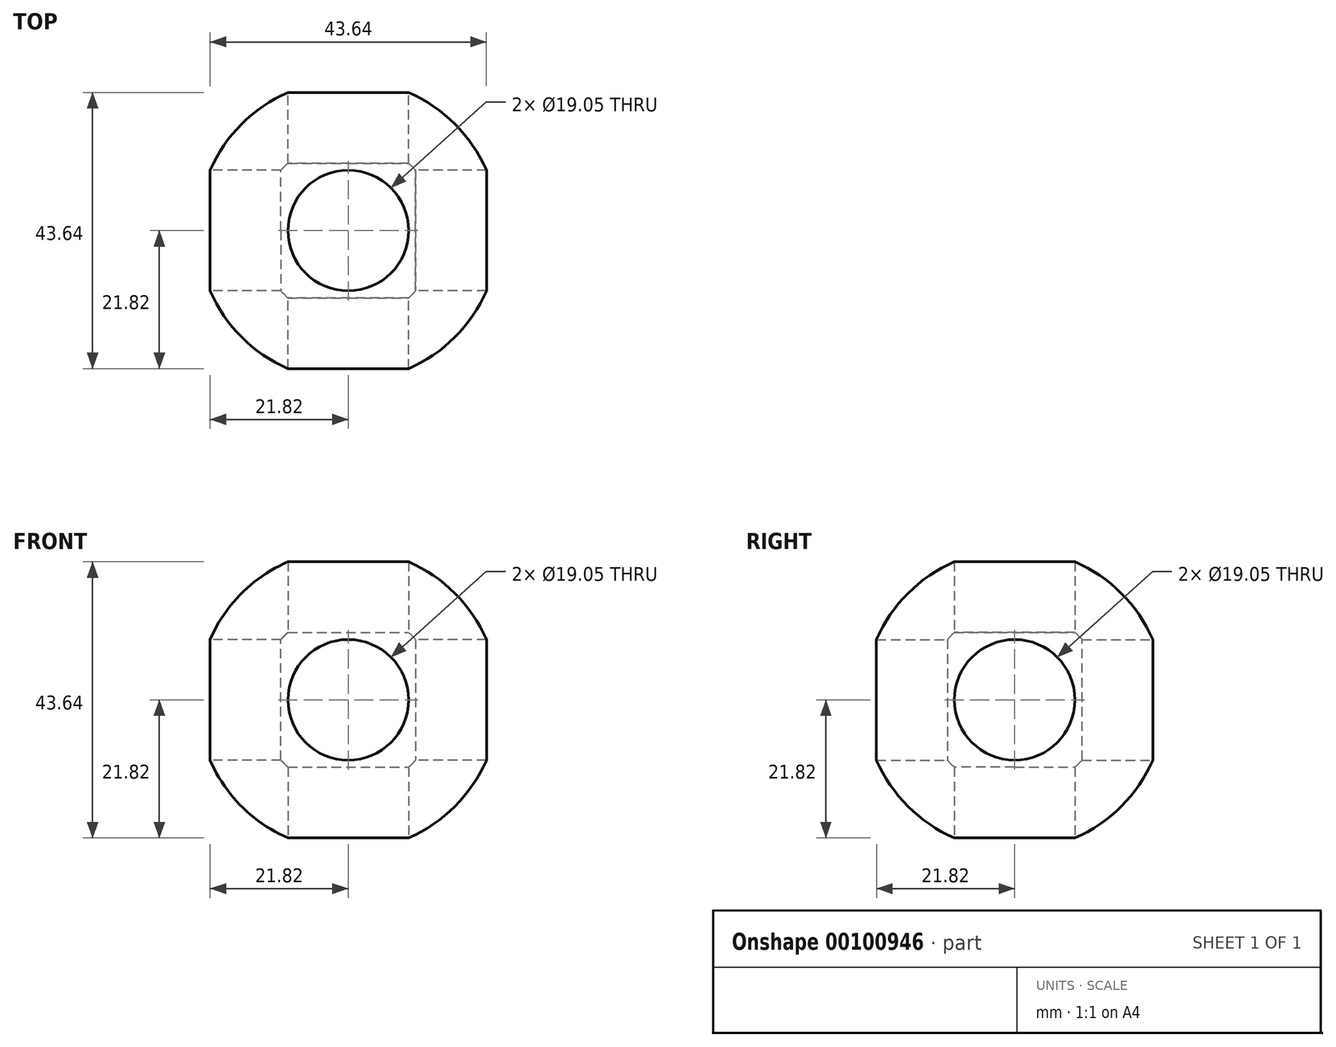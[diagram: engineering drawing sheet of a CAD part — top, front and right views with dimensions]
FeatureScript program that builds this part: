
annotation { "Feature Type Name" : "Feature", "Feature Type Description" : "" }
export const myFeature = defineFeature(function(context is Context, id is Id, definition is map)
    precondition{}
    {
        {
            var Q0;
            Q0=qCreatedBy(makeId("Front.planeOp"),FACE);
            var sketch = newSketch(context, id + "F0", { "sketchPlane" : qUnion([Q0])});
            skArc(sketch, "E0", {"start": v(0, -23.81) * mm, "mid": v(23.81, 0) * mm, "end": v(0, 23.81) * mm});
            skLineSegment(sketch, "E1", {"start": v(0, 23.81) * mm, "end": v(0, -23.81) * mm});
            skSolve(sketch);
        }
        {
            var Q0;
            Q0 = qSketchRegion(id + "F0", true);
            var Q1;
            Q1=sQuery(id+"F0.wireOp",EDGE,"E1");
            revolve(context, id + "F1", {"entities" : qUnion([Q0]), "axis" : qUnion([Q1]), "revolveType" : RevolveType.FULL});
        }
        {
            var Q0;
            Q0=qCreatedBy(makeId("Front.planeOp"),FACE);
            var sketch = newSketch(context, id + "F2", { "sketchPlane" : qUnion([Q0])});
            skArc(sketch, "E2", {"start": v(0, -14.28) * mm, "mid": v(14.28, 0) * mm, "end": v(0, 14.28) * mm});
            skLineSegment(sketch, "E3", {"start": v(0, 14.28) * mm, "end": v(0, -14.28) * mm});
            skSolve(sketch);
        }
        {
            var Q0;
            Q0 = qSketchRegion(id + "F2", true);
            var Q1;
            Q1=sQuery(id+"F2.wireOp",EDGE,"E3");
            revolve(context, id + "F3", {"operationType" : NewBodyOperationType.REMOVE, "entities" : qUnion([Q0]), "axis" : qUnion([Q1]), "revolveType" : RevolveType.FULL, "oppositeDirection" : true});
        }
        {
            var Q0;
            Q0=qCreatedBy(makeId("Front.planeOp"),FACE);
            var sketch = newSketch(context, id + "F4", { "sketchPlane" : qUnion([Q0])});
            skCircle(sketch, "E4", {"center": v(0, 0) * mm, "radius": 9.53 * mm});
            skSolve(sketch);
        }
        {
            var Q0;
            Q0 = qSketchRegion(id + "F4", true);
            extrude(context, id + "F5", {"entities" : qUnion([Q0]), "operationType" : NewBodyOperationType.REMOVE, "endBound" : BoundingType.SYMMETRIC, "depth" : 58.74 * mm});
        }
        {
            var Q0;
            Q0=qCreatedBy(makeId("Right.planeOp"),FACE);
            var sketch = newSketch(context, id + "F6", { "sketchPlane" : qUnion([Q0])});
            skCircle(sketch, "E5", {"center": v(0, 0) * mm, "radius": 9.53 * mm});
            skSolve(sketch);
        }
        {
            var Q0;
            Q0 = qSketchRegion(id + "F6", true);
            extrude(context, id + "F7", {"entities" : qUnion([Q0]), "operationType" : NewBodyOperationType.REMOVE, "endBound" : BoundingType.SYMMETRIC, "depth" : 58.74 * mm});
        }
        {
            var Q0;
            Q0=qCreatedBy(makeId("Top.planeOp"),FACE);
            var sketch = newSketch(context, id + "F8", { "sketchPlane" : qUnion([Q0])});
            skCircle(sketch, "E6", {"center": v(0, 0) * mm, "radius": 9.52 * mm});
            skSolve(sketch);
        }
        {
            var Q0;
            Q0 = qSketchRegion(id + "F8", true);
            extrude(context, id + "F9", {"entities" : qUnion([Q0]), "operationType" : NewBodyOperationType.REMOVE, "endBound" : BoundingType.SYMMETRIC, "depth" : 58.74 * mm});
        }
    });
